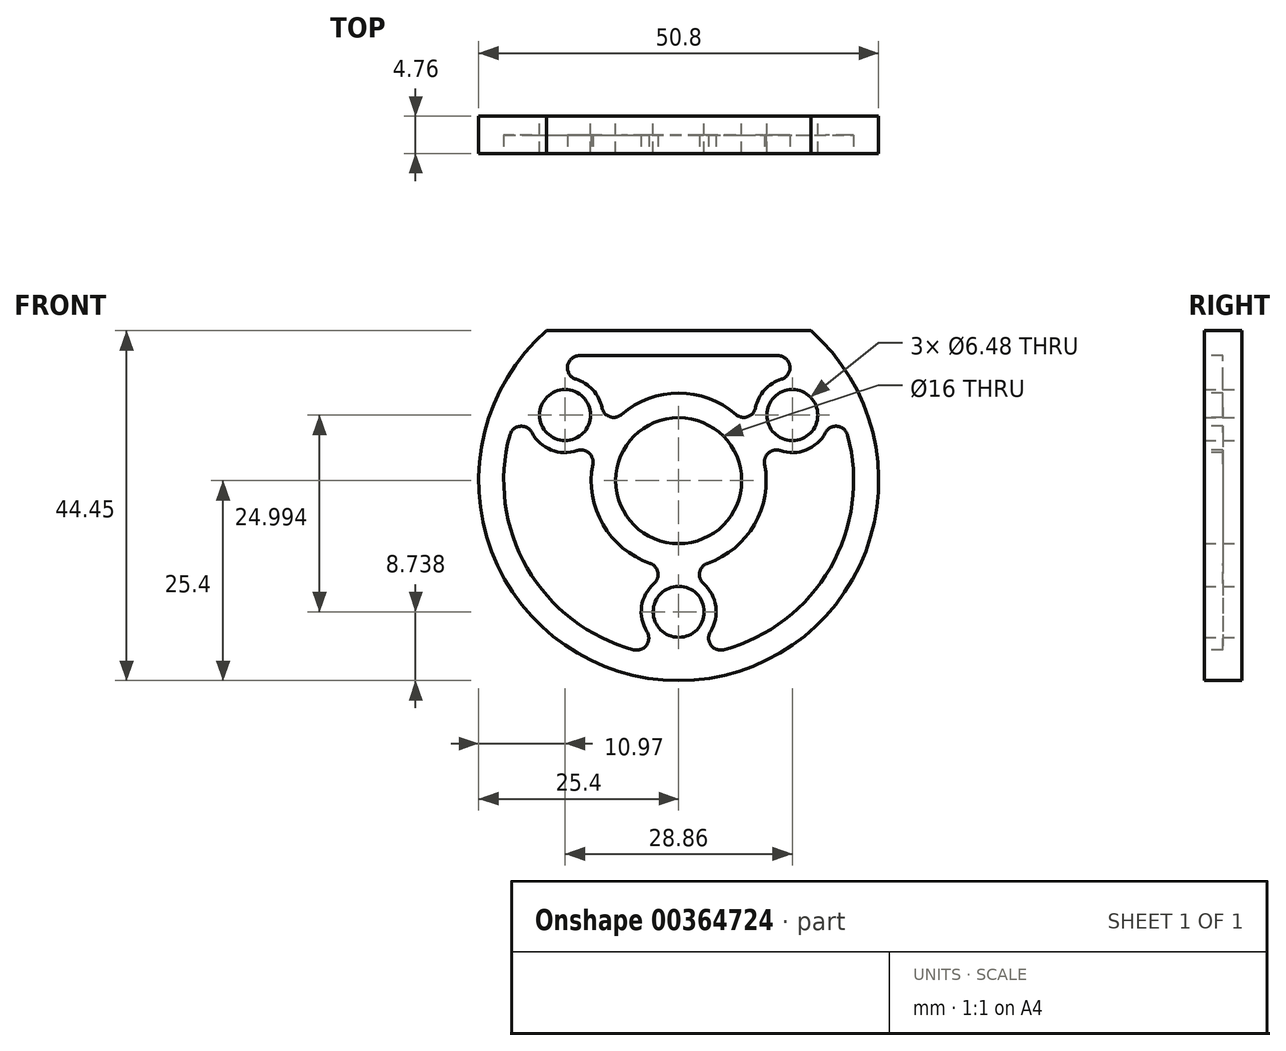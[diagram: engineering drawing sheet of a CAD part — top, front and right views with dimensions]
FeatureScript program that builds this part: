
annotation { "Feature Type Name" : "Feature", "Feature Type Description" : "" }
export const myFeature = defineFeature(function(context is Context, id is Id, definition is map)
    precondition{}
    {
        {
            var Q0;
            Q0=qCreatedBy(makeId("Front.planeOp"),FACE);
            var sketch = newSketch(context, id + "F0", { "sketchPlane" : qUnion([Q0])});
            skCircle(sketch, "E0", {"center": v(0, 0) * mm, "radius": 16.66 * mm, "construction": true});
            skCircle(sketch, "E1", {"center": v(-14.43, 8.33) * mm, "radius": 3.24 * mm});
            skCircle(sketch, "E2", {"center": v(14.43, 8.33) * mm, "radius": 3.24 * mm});
            skCircle(sketch, "E3", {"center": v(0, -16.66) * mm, "radius": 3.24 * mm});
            skCircle(sketch, "E4", {"center": v(0, 0) * mm, "radius": 25.4 * mm});
            skCircle(sketch, "E5", {"center": v(0, 0) * mm, "radius": 8 * mm});
            skLineSegment(sketch, "E6", {"start": v(-14.43, 8.33) * mm, "end": v(0, -16.66) * mm, "construction": true});
            skLineSegment(sketch, "E7", {"start": v(14.43, 8.33) * mm, "end": v(0, -16.66) * mm, "construction": true});
            skLineSegment(sketch, "E8", {"start": v(14.43, 8.33) * mm, "end": v(-14.43, 8.33) * mm, "construction": true});
            skSolve(sketch);
        }
        {
            var Q0;
            Q0 = qSketchRegion(id + "F0", true);
            extrude(context, id + "F1", {"entities" : qUnion([Q0]), "depth" : 4.76 * mm});
        }
        {
            var Q0;
            Q0=makeQuery(id+"F1.opExtrude","CAP_FACE",FACE,{"disambiguationData":[OSD([sQuery(id+"F0.wireOp",EDGE,"E1"),sQuery(id+"F0.wireOp",EDGE,"E2"),sQuery(id+"F0.wireOp",EDGE,"E3"),sQuery(id+"F0.wireOp",EDGE,"E4"),sQuery(id+"F0.wireOp",EDGE,"E5")])],"isStart":false});
            var sketch = newSketch(context, id + "F2", { "sketchPlane" : qUnion([Q0])});
            skLineSegment(sketch, "E9.bottom", {"start": v(-24.52, 33.4) * mm, "end": v(26.04, 33.4) * mm});
            skLineSegment(sketch, "E9.top", {"start": v(-24.52, 19.05) * mm, "end": v(26.04, 19.05) * mm});
            skLineSegment(sketch, "E9.left", {"start": v(-24.52, 33.4) * mm, "end": v(-24.52, 19.05) * mm});
            skLineSegment(sketch, "E9.right", {"start": v(26.04, 33.4) * mm, "end": v(26.04, 19.05) * mm});
            skSolve(sketch);
        }
        {
            var Q0;
            Q0 = qSketchRegion(id + "F2", true);
            extrude(context, id + "F3", {"entities" : qUnion([Q0]), "operationType" : NewBodyOperationType.REMOVE, "oppositeDirection" : true, "depth" : 25.4 * mm});
        }
        {
            var Q0;
            Q0=makeQuery(id+"F1.opExtrude","CAP_FACE",FACE,{"disambiguationData":[OSD([sQuery(id+"F0.wireOp",EDGE,"E1"),sQuery(id+"F0.wireOp",EDGE,"E2"),sQuery(id+"F0.wireOp",EDGE,"E3"),sQuery(id+"F0.wireOp",EDGE,"E4"),sQuery(id+"F0.wireOp",EDGE,"E5")])],"isStart":false});
            var sketch = newSketch(context, id + "F4", { "sketchPlane" : qUnion([Q0])});
            skArc(sketch, "E10", {"start": v(-10.91, 2.1) * mm, "mid": v(-9.62, -5.56) * mm, "end": v(-3.65, -10.5) * mm});
            skArc(sketch, "E11", {"start": v(7.27, 8.4) * mm, "mid": v(0, 11.11) * mm, "end": v(-7.27, 8.4) * mm});
            skArc(sketch, "E12", {"start": v(3.65, -10.5) * mm, "mid": v(9.62, -5.56) * mm, "end": v(10.91, 2.1) * mm});
            skArc(sketch, "E13", {"start": v(-9.76, 9.26) * mm, "mid": v(-10.9, 11.53) * mm, "end": v(-13.06, 12.9) * mm});
            skArc(sketch, "E14", {"start": v(-18.64, 6.1) * mm, "mid": v(-16.2, 3.9) * mm, "end": v(-12.9, 3.82) * mm});
            skArc(sketch, "E15", {"start": v(-21.46, 5.79) * mm, "mid": v(-19.25, -11.11) * mm, "end": v(-5.72, -21.48) * mm});
            skArc(sketch, "E16", {"start": v(5.72, -21.48) * mm, "mid": v(19.25, -11.11) * mm, "end": v(21.46, 5.79) * mm});
            skArc(sketch, "E17.filletArc", {"start": v(-10.91, 2.1) * mm, "mid": v(-11.4, 3.53) * mm, "end": v(-12.9, 3.82) * mm});
            skArc(sketch, "E18.filletArc", {"start": v(-18.64, 6.1) * mm, "mid": v(-20.16, 6.9) * mm, "end": v(-21.46, 5.79) * mm});
            skArc(sketch, "E19.filletArc", {"start": v(-9.76, 9.26) * mm, "mid": v(-8.76, 8.12) * mm, "end": v(-7.27, 8.4) * mm});
            skArc(sketch, "E20", {"start": v(12.9, 3.82) * mm, "mid": v(16.2, 3.9) * mm, "end": v(18.64, 6.1) * mm});
            skArc(sketch, "E21", {"start": v(13.06, 12.9) * mm, "mid": v(10.9, 11.53) * mm, "end": v(9.76, 9.26) * mm});
            skArc(sketch, "E22", {"start": v(4.03, -19.2) * mm, "mid": v(4.71, -15.97) * mm, "end": v(3.14, -13.08) * mm});
            skArc(sketch, "E23", {"start": v(-3.14, -13.08) * mm, "mid": v(-4.71, -15.97) * mm, "end": v(-4.03, -19.2) * mm});
            skArc(sketch, "E24.filletArc", {"start": v(-5.72, -21.48) * mm, "mid": v(-4.1, -20.9) * mm, "end": v(-4.03, -19.2) * mm});
            skArc(sketch, "E25.filletArc", {"start": v(-3.14, -13.08) * mm, "mid": v(-2.65, -11.64) * mm, "end": v(-3.65, -10.5) * mm});
            skArc(sketch, "E26.filletArc", {"start": v(4.03, -19.2) * mm, "mid": v(4.1, -20.9) * mm, "end": v(5.72, -21.48) * mm});
            skArc(sketch, "E27.filletArc", {"start": v(3.65, -10.5) * mm, "mid": v(2.65, -11.64) * mm, "end": v(3.14, -13.08) * mm});
            skArc(sketch, "E28.filletArc", {"start": v(21.46, 5.79) * mm, "mid": v(20.16, 6.9) * mm, "end": v(18.64, 6.1) * mm});
            skArc(sketch, "E29.filletArc", {"start": v(12.9, 3.82) * mm, "mid": v(11.4, 3.53) * mm, "end": v(10.91, 2.1) * mm});
            skArc(sketch, "E30.filletArc", {"start": v(7.27, 8.4) * mm, "mid": v(8.76, 8.12) * mm, "end": v(9.76, 9.26) * mm});
            skLineSegment(sketch, "E31", {"start": v(-12.62, 15.88) * mm, "end": v(12.62, 15.88) * mm});
            skArc(sketch, "E32.filletArc", {"start": v(-12.62, 15.88) * mm, "mid": v(-14.13, 14.57) * mm, "end": v(-13.06, 12.9) * mm});
            skArc(sketch, "E33.filletArc", {"start": v(13.06, 12.9) * mm, "mid": v(14.13, 14.57) * mm, "end": v(12.62, 15.88) * mm});
            skSolve(sketch);
        }
        {
            var Q0;
            Q0 = qSketchRegion(id + "F4", true);
            extrude(context, id + "F5", {"entities" : qUnion([Q0]), "operationType" : NewBodyOperationType.REMOVE, "oppositeDirection" : true, "depth" : 2.38 * mm, "offsetDistance" : 25.4 * mm});
        }
    });
